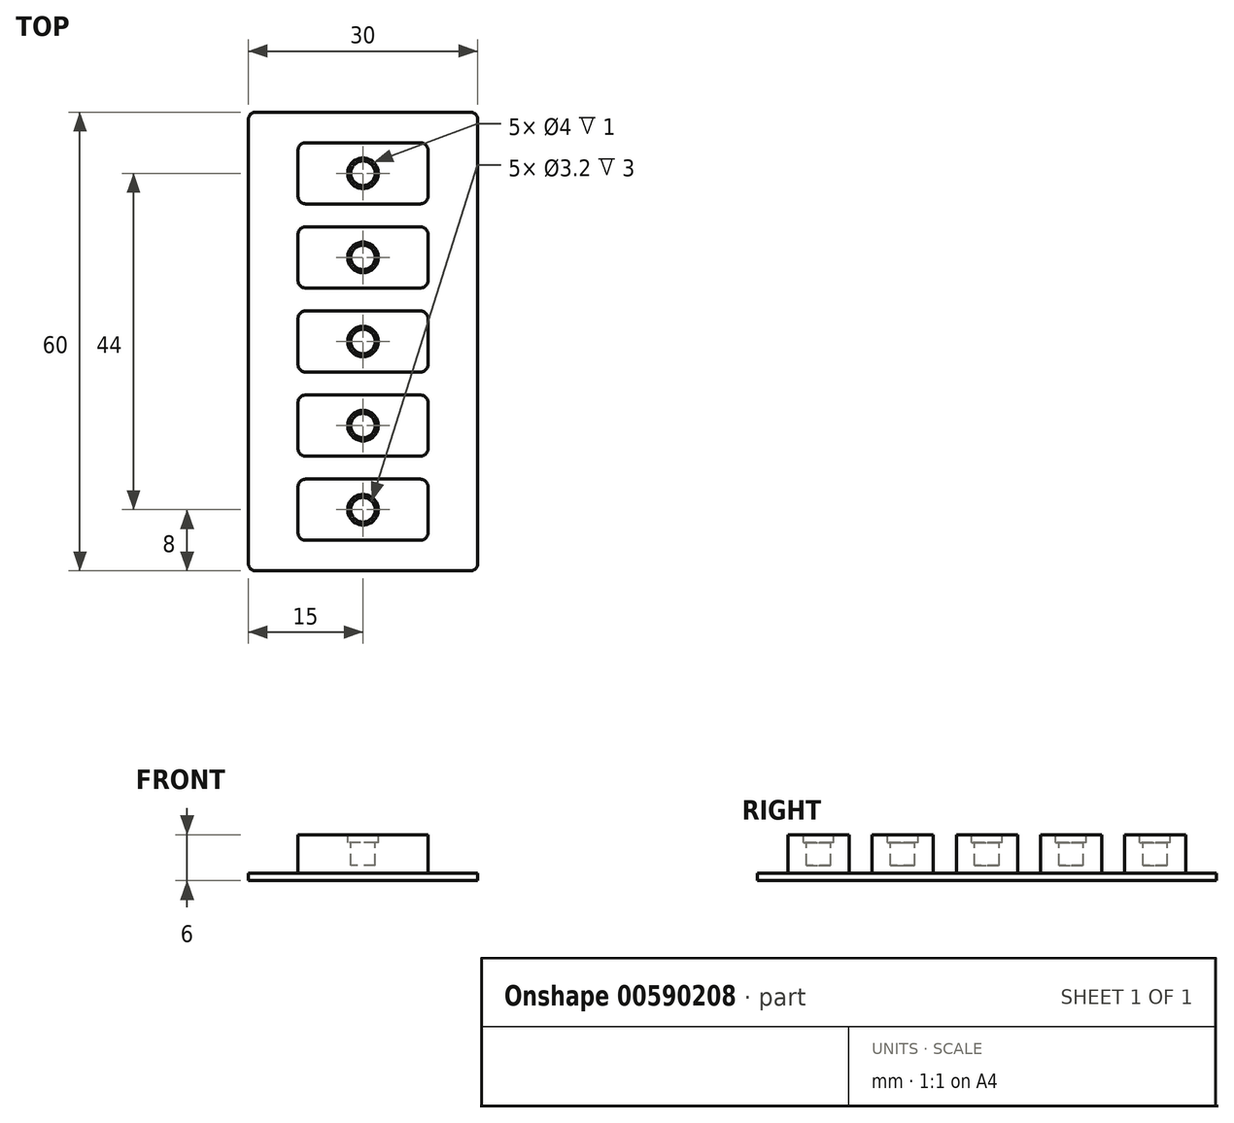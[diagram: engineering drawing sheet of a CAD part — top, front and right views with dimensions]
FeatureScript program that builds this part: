
annotation { "Feature Type Name" : "Feature", "Feature Type Description" : "" }
export const myFeature = defineFeature(function(context is Context, id is Id, definition is map)
    precondition{}
    {
        {
            var Q0;
            Q0=qCreatedBy(makeId("Top.planeOp"),FACE);
            var sketch = newSketch(context, id + "F0", { "sketchPlane" : qUnion([Q0])});
            skLineSegment(sketch, "E0.bottom", {"start": v(-15, 30) * mm, "end": v(15, 30) * mm});
            skLineSegment(sketch, "E0.top", {"start": v(-15, -30) * mm, "end": v(15, -30) * mm});
            skLineSegment(sketch, "E0.left", {"start": v(-15, 30) * mm, "end": v(-15, -30) * mm});
            skLineSegment(sketch, "E0.right", {"start": v(15, 30) * mm, "end": v(15, -30) * mm});
            skPoint(sketch, "E0.middle", {"position": v(0, 0) * mm});
            skSolve(sketch);
        }
        {
            var Q0;
            Q0 = qSketchRegion(id + "F0", true);
            extrude(context, id + "F1", {"entities" : qUnion([Q0]), "oppositeDirection" : true, "depth" : 1 * mm, "offsetDistance" : 25 * mm});
        }
        {
            var Q0;
            Q0=qCreatedBy(makeId("Top.planeOp"),FACE);
            var sketch = newSketch(context, id + "F2", { "sketchPlane" : qUnion([Q0])});
            skLineSegment(sketch, "E1.bottom", {"start": v(-8.5, 4) * mm, "end": v(8.5, 4) * mm});
            skLineSegment(sketch, "E1.top", {"start": v(-8.5, -4) * mm, "end": v(8.5, -4) * mm});
            skLineSegment(sketch, "E1.left", {"start": v(-8.5, 4) * mm, "end": v(-8.5, -4) * mm});
            skLineSegment(sketch, "E1.right", {"start": v(8.5, 4) * mm, "end": v(8.5, -4) * mm});
            skPoint(sketch, "E1.middle", {"position": v(0, 0) * mm});
            skLineSegment(sketch, "E2.bottom", {"start": v(-8.5, -15) * mm, "end": v(8.5, -15) * mm});
            skLineSegment(sketch, "E2.top", {"start": v(-8.5, -7) * mm, "end": v(8.5, -7) * mm});
            skLineSegment(sketch, "E2.left", {"start": v(-8.5, -15) * mm, "end": v(-8.5, -7) * mm});
            skLineSegment(sketch, "E2.right", {"start": v(8.5, -15) * mm, "end": v(8.5, -7) * mm});
            skPoint(sketch, "E2.middle", {"position": v(0, -11) * mm});
            skLineSegment(sketch, "E3.bottom", {"start": v(-8.5, 15) * mm, "end": v(8.5, 15) * mm});
            skLineSegment(sketch, "E3.top", {"start": v(-8.5, 7) * mm, "end": v(8.5, 7) * mm});
            skLineSegment(sketch, "E3.left", {"start": v(-8.5, 15) * mm, "end": v(-8.5, 7) * mm});
            skLineSegment(sketch, "E3.right", {"start": v(8.5, 15) * mm, "end": v(8.5, 7) * mm});
            skPoint(sketch, "E3.middle", {"position": v(0, 11) * mm});
            skLineSegment(sketch, "E4.bottom", {"start": v(8.5, -18) * mm, "end": v(-8.5, -18) * mm});
            skLineSegment(sketch, "E4.top", {"start": v(8.5, -26) * mm, "end": v(-8.5, -26) * mm});
            skLineSegment(sketch, "E4.left", {"start": v(8.5, -18) * mm, "end": v(8.5, -26) * mm});
            skLineSegment(sketch, "E4.right", {"start": v(-8.5, -18) * mm, "end": v(-8.5, -26) * mm});
            skPoint(sketch, "E4.middle", {"position": v(0, -22) * mm});
            skLineSegment(sketch, "E5.bottom", {"start": v(8.5, 26) * mm, "end": v(-8.5, 26) * mm});
            skLineSegment(sketch, "E5.top", {"start": v(8.5, 18) * mm, "end": v(-8.5, 18) * mm});
            skLineSegment(sketch, "E5.left", {"start": v(8.5, 26) * mm, "end": v(8.5, 18) * mm});
            skLineSegment(sketch, "E5.right", {"start": v(-8.5, 26) * mm, "end": v(-8.5, 18) * mm});
            skPoint(sketch, "E5.middle", {"position": v(0, 22) * mm});
            skSolve(sketch);
        }
        {
            var Q0;
            Q0=qSketchRegion(id+"F2",true);
            extrude(context, id + "F3", {"entities" : qUnion([Q0]), "operationType" : NewBodyOperationType.ADD, "depth" : 5 * mm, "offsetDistance" : 25 * mm});
        }
        {
            var Q0;
            Q0=makeQuery(id+"F3.opExtrude","CAP_FACE",FACE,{"disambiguationData":[OSD([sQuery(id+"F2.wireOp",EDGE,"E3.bottom"),sQuery(id+"F2.wireOp",EDGE,"E3.top"),sQuery(id+"F2.wireOp",EDGE,"E3.left"),sQuery(id+"F2.wireOp",EDGE,"E3.right")])],"isStart":false});
            var sketch = newSketch(context, id + "F4", { "sketchPlane" : qUnion([Q0])});
            skCircle(sketch, "E6", {"center": v(0, 0) * mm, "radius": 2 * mm});
            skCircle(sketch, "E7", {"center": v(0, 11) * mm, "radius": 2 * mm});
            skCircle(sketch, "E8", {"center": v(0, 22) * mm, "radius": 2 * mm});
            skCircle(sketch, "E9", {"center": v(0, -11) * mm, "radius": 2 * mm});
            skCircle(sketch, "E10", {"center": v(0, -22) * mm, "radius": 2 * mm});
            skSolve(sketch);
        }
        {
            var Q0;
            Q0=qSketchRegion(id+"F4",true);
            extrude(context, id + "F5", {"entities" : qUnion([Q0]), "operationType" : NewBodyOperationType.REMOVE, "oppositeDirection" : true, "depth" : 1 * mm, "offsetDistance" : 25 * mm});
        }
        {
            var Q0;
            Q0=makeQuery(id+"F3.opExtrude","SWEPT_EDGE",EDGE,{"disambiguationData":[OSD([sQuery(id+"F2.wireOp",EDGE,"E1.bottom"),sQuery(id+"F2.wireOp",EDGE,"E1.left")])]});
            var Q1;
            Q1=makeQuery(id+"F3.opExtrude","SWEPT_EDGE",EDGE,{"disambiguationData":[OSD([sQuery(id+"F2.wireOp",EDGE,"E1.bottom"),sQuery(id+"F2.wireOp",EDGE,"E1.right")])]});
            var Q2;
            Q2=makeQuery(id+"F3.opExtrude","SWEPT_EDGE",EDGE,{"disambiguationData":[OSD([sQuery(id+"F2.wireOp",EDGE,"E1.top"),sQuery(id+"F2.wireOp",EDGE,"E1.right")])]});
            var Q3;
            Q3=makeQuery(id+"F3.opExtrude","SWEPT_EDGE",EDGE,{"disambiguationData":[OSD([sQuery(id+"F2.wireOp",EDGE,"E1.top"),sQuery(id+"F2.wireOp",EDGE,"E1.left")])]});
            var Q4;
            Q4=makeQuery(id+"F1.opExtrude","SWEPT_EDGE",EDGE,{"disambiguationData":[OSD([sQuery(id+"F0.wireOp",EDGE,"E0.bottom"),sQuery(id+"F0.wireOp",EDGE,"E0.left")])]});
            var Q5;
            Q5=makeQuery(id+"F1.opExtrude","SWEPT_EDGE",EDGE,{"disambiguationData":[OSD([sQuery(id+"F0.wireOp",EDGE,"E0.bottom"),sQuery(id+"F0.wireOp",EDGE,"E0.right")])]});
            var Q6;
            Q6=makeQuery(id+"F1.opExtrude","SWEPT_EDGE",EDGE,{"disambiguationData":[OSD([sQuery(id+"F0.wireOp",EDGE,"E0.top"),sQuery(id+"F0.wireOp",EDGE,"E0.right")])]});
            var Q7;
            Q7=makeQuery(id+"F1.opExtrude","SWEPT_EDGE",EDGE,{"disambiguationData":[OSD([sQuery(id+"F0.wireOp",EDGE,"E0.top"),sQuery(id+"F0.wireOp",EDGE,"E0.left")])]});
            var Q8;
            Q8=makeQuery(id+"F3.opExtrude","SWEPT_EDGE",EDGE,{"disambiguationData":[OSD([sQuery(id+"F2.wireOp",EDGE,"E4.top"),sQuery(id+"F2.wireOp",EDGE,"E4.right")])]});
            var Q9;
            Q9=makeQuery(id+"F3.opExtrude","SWEPT_EDGE",EDGE,{"disambiguationData":[OSD([sQuery(id+"F2.wireOp",EDGE,"E2.bottom"),sQuery(id+"F2.wireOp",EDGE,"E2.left")])]});
            var Q10;
            Q10=makeQuery(id+"F3.opExtrude","SWEPT_EDGE",EDGE,{"disambiguationData":[OSD([sQuery(id+"F2.wireOp",EDGE,"E2.top"),sQuery(id+"F2.wireOp",EDGE,"E2.left")])]});
            var Q11;
            Q11=makeQuery(id+"F3.opExtrude","SWEPT_EDGE",EDGE,{"disambiguationData":[OSD([sQuery(id+"F2.wireOp",EDGE,"E3.top"),sQuery(id+"F2.wireOp",EDGE,"E3.left")])]});
            var Q12;
            Q12=makeQuery(id+"F3.opExtrude","SWEPT_EDGE",EDGE,{"disambiguationData":[OSD([sQuery(id+"F2.wireOp",EDGE,"E3.bottom"),sQuery(id+"F2.wireOp",EDGE,"E3.left")])]});
            var Q13;
            Q13=makeQuery(id+"F3.opExtrude","SWEPT_EDGE",EDGE,{"disambiguationData":[OSD([sQuery(id+"F2.wireOp",EDGE,"E5.top"),sQuery(id+"F2.wireOp",EDGE,"E5.right")])]});
            var Q14;
            Q14=makeQuery(id+"F3.opExtrude","SWEPT_EDGE",EDGE,{"disambiguationData":[OSD([sQuery(id+"F2.wireOp",EDGE,"E5.bottom"),sQuery(id+"F2.wireOp",EDGE,"E5.right")])]});
            var Q15;
            Q15=makeQuery(id+"F3.opExtrude","SWEPT_EDGE",EDGE,{"disambiguationData":[OSD([sQuery(id+"F2.wireOp",EDGE,"E4.bottom"),sQuery(id+"F2.wireOp",EDGE,"E4.right")])]});
            var Q16;
            Q16=makeQuery(id+"F3.opExtrude","SWEPT_EDGE",EDGE,{"disambiguationData":[OSD([sQuery(id+"F2.wireOp",EDGE,"E4.top"),sQuery(id+"F2.wireOp",EDGE,"E4.left")])]});
            var Q17;
            Q17=makeQuery(id+"F3.opExtrude","SWEPT_EDGE",EDGE,{"disambiguationData":[OSD([sQuery(id+"F2.wireOp",EDGE,"E4.bottom"),sQuery(id+"F2.wireOp",EDGE,"E4.left")])]});
            var Q18;
            Q18=makeQuery(id+"F3.opExtrude","SWEPT_EDGE",EDGE,{"disambiguationData":[OSD([sQuery(id+"F2.wireOp",EDGE,"E2.bottom"),sQuery(id+"F2.wireOp",EDGE,"E2.right")])]});
            var Q19;
            Q19=makeQuery(id+"F3.opExtrude","SWEPT_EDGE",EDGE,{"disambiguationData":[OSD([sQuery(id+"F2.wireOp",EDGE,"E2.top"),sQuery(id+"F2.wireOp",EDGE,"E2.right")])]});
            var Q20;
            Q20=makeQuery(id+"F3.opExtrude","SWEPT_EDGE",EDGE,{"disambiguationData":[OSD([sQuery(id+"F2.wireOp",EDGE,"E3.top"),sQuery(id+"F2.wireOp",EDGE,"E3.right")])]});
            var Q21;
            Q21=makeQuery(id+"F3.opExtrude","SWEPT_EDGE",EDGE,{"disambiguationData":[OSD([sQuery(id+"F2.wireOp",EDGE,"E3.bottom"),sQuery(id+"F2.wireOp",EDGE,"E3.right")])]});
            var Q22;
            Q22=makeQuery(id+"F3.opExtrude","SWEPT_EDGE",EDGE,{"disambiguationData":[OSD([sQuery(id+"F2.wireOp",EDGE,"E5.top"),sQuery(id+"F2.wireOp",EDGE,"E5.left")])]});
            var Q23;
            Q23=makeQuery(id+"F3.opExtrude","SWEPT_EDGE",EDGE,{"disambiguationData":[OSD([sQuery(id+"F2.wireOp",EDGE,"E5.bottom"),sQuery(id+"F2.wireOp",EDGE,"E5.left")])]});
            fillet(context, id + "F6", {"entities" : qUnion([Q0, Q1, Q2, Q3, Q4, Q5, Q6, Q7, Q8, Q9, Q10, Q11, Q12, Q13, Q14, Q15, Q16, Q17, Q18, Q19, Q20, Q21, Q22, Q23]), "radius" : 1 * mm, "tangentPropagation" : true, "allowEdgeOverflow" : false});
        }
        {
            var Q0;
            Q0=makeQuery(id+"F5.boolean.opBoolean","COPY",FACE,{"derivedFrom":makeQuery(id+"F5.opExtrude","CAP_FACE",FACE,{"disambiguationData":[OSD([sQuery(id+"F4.wireOp",EDGE,"E6")])],"isStart":false})});
            var sketch = newSketch(context, id + "F7", { "sketchPlane" : qUnion([Q0])});
            skCircle(sketch, "E11", {"center": v(0, 0) * mm, "radius": 1.6 * mm});
            skCircle(sketch, "E12", {"center": v(0, -11) * mm, "radius": 1.6 * mm});
            skCircle(sketch, "E13", {"center": v(0, -22) * mm, "radius": 1.6 * mm});
            skCircle(sketch, "E14", {"center": v(0, 11) * mm, "radius": 1.6 * mm});
            skCircle(sketch, "E15", {"center": v(0, 22) * mm, "radius": 1.6 * mm});
            skSolve(sketch);
        }
        {
            var Q0;
            Q0 = qSketchRegion(id + "F7", true);
            extrude(context, id + "F8", {"entities" : qUnion([Q0]), "operationType" : NewBodyOperationType.REMOVE, "oppositeDirection" : true, "depth" : 3 * mm, "offsetDistance" : 25 * mm});
        }
    });
